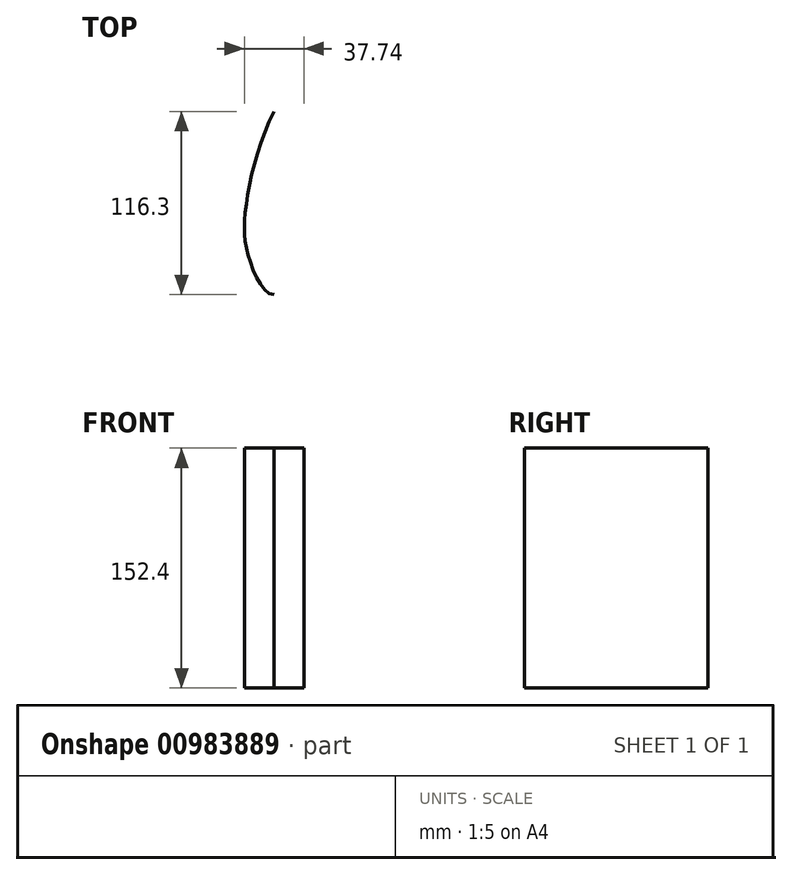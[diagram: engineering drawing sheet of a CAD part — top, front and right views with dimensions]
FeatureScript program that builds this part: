
annotation { "Feature Type Name" : "Feature", "Feature Type Description" : "" }
export const myFeature = defineFeature(function(context is Context, id is Id, definition is map)
    precondition{}
    {
        {
            var Q0;
            Q0=qCreatedBy(makeId("Top.planeOp"),FACE);
            var sketch = newSketch(context, id + "F0", { "sketchPlane" : qUnion([Q0])});
            skFitSpline(sketch, "E0", {"points": [v(0, -46.87) * mm, v(-15.7, -24.54) * mm, v(-18.26, 5.47) * mm, v(0, 69.43) * mm], "startDerivative": vector(-74.34, -2.52) * mm, "endDerivative": vector(75.1, 143) * mm});
            skFitSpline(sketch, "E1.MirrorCS", {"points": [v(0, -46.87) * mm, v(15.7, -24.54) * mm, v(18.26, 5.47) * mm, v(0, 69.43) * mm], "startDerivative": vector(74.34, -2.52) * mm, "endDerivative": vector(-75.1, 143) * mm});
            skSolve(sketch);
        }
        {
            var Q0;
            Q0=makeQuery(id+"F0.imprint","IMPRINT",FACE,{"disambiguationData":[TD([[makeQuery(id+"F0.imprint","IMPRINT",EDGE,{"derivedFrom":sQuery(id+"F0.wireOp",EDGE,"E0")}),-1.0]])]});
            var Q1;
            Q1=sQuery(id+"F0.wireOp",EDGE,"E0");
            var Q2;
            Q2=sQuery(id+"F0.wireOp",EDGE,"E1.MirrorCS");
            extrude(context, id + "F1", {"entities" : qUnion([Q0]), "bodyType" : ToolBodyType.SURFACE, "surfaceEntities" : qUnion([Q1, Q2]), "oppositeDirection" : true, "depth" : 152.4 * mm, "offsetDistance" : 25.4 * mm});
        }
    });
